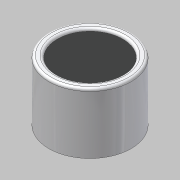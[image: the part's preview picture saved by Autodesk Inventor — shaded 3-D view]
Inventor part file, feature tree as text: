
AUTODESK INVENTOR PART (.ipt)
format: ipt  version: 2012 (Build 160160000, 160)  size: 108,544 bytes
history: native  units: mm (DEFAULTED — no unit token found)
features: sketch x2, extrude x1, hole x1, fillet x1
ambient origin geometry x8: Origin, YZ Plane, XZ Plane, XY Plane, X Axis, Y Axis, Z Axis, Center Point
bodies: Solid1 (feature_tree)
feature tree (5):
  extrude  "Extrusion1"  Depth=12.0mm TaperAngle=0.0deg
  hole  "Hole1"  [1 undecoded]
  fillet  "Fillet1"  [1 undecoded]
  sketch  "Sketch1"  dims[d0=16.3mm d1=12.0mm d2=0.0mm]
  sketch  "Sketch2"  dims[d3=13.0mm d4=6.0mm d5=4.0mm d6=2.0mm d7=14.3117mm d8=0.5mm d9=0.0mm d10=0.5mm]
note: 2 required parameter values undecoded (feature->parameter linkage not recoverable at this tier; creation-order binding heuristic only, values carry confidence <= 0.55)
